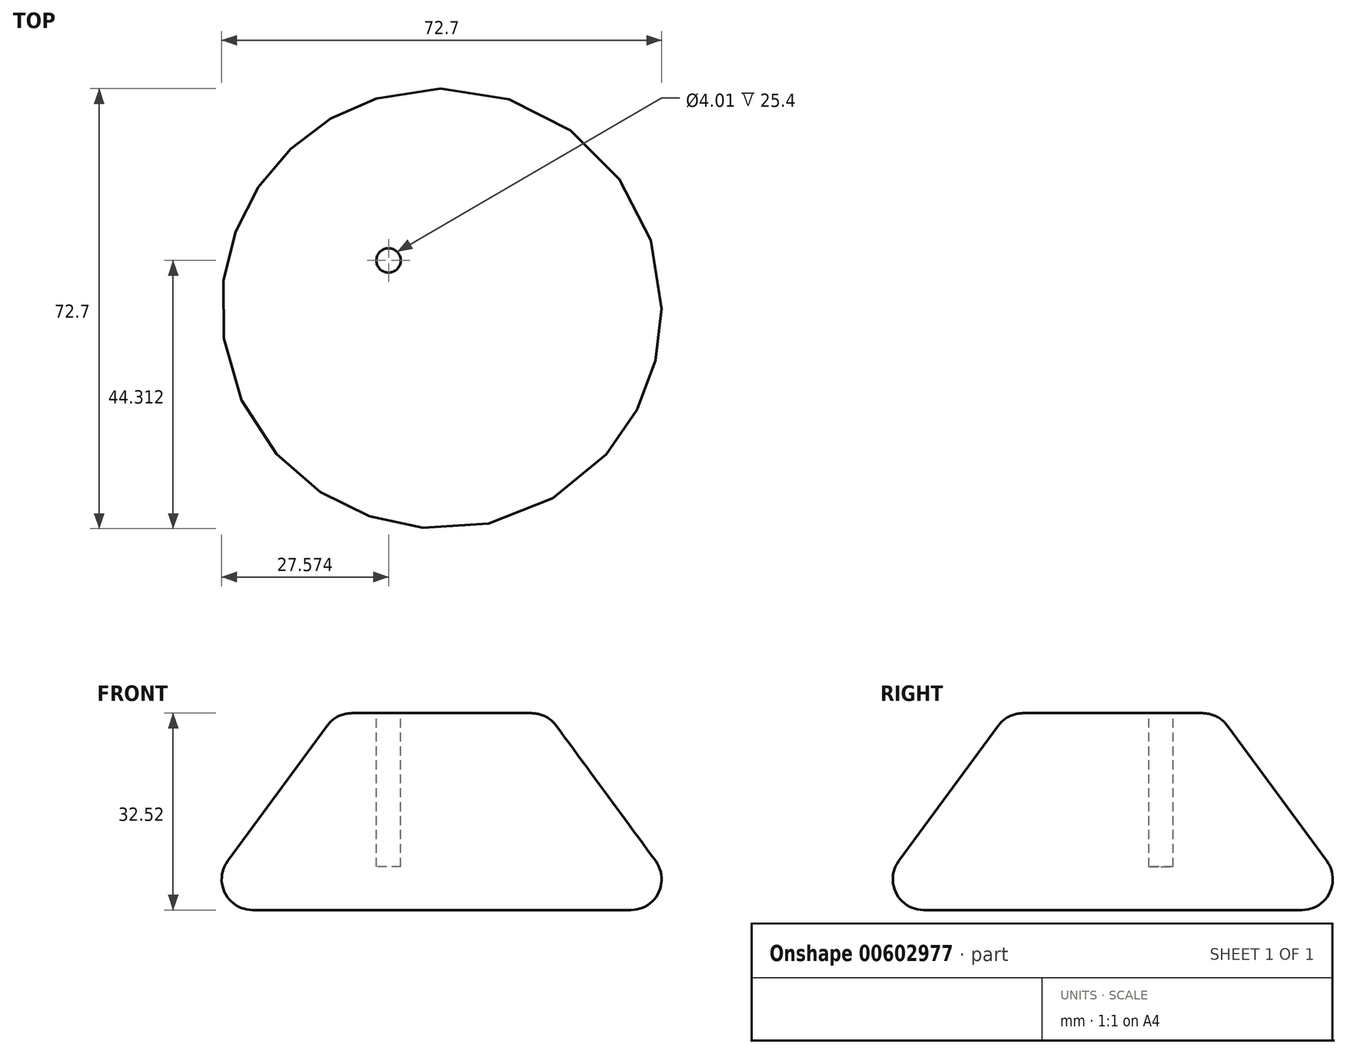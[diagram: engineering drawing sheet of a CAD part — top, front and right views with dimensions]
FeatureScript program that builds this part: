
annotation { "Feature Type Name" : "Feature", "Feature Type Description" : "" }
export const myFeature = defineFeature(function(context is Context, id is Id, definition is map)
    precondition{}
    {
        {
            var Q0;
            Q0=qCreatedBy(makeId("Front.planeOp"),FACE);
            var sketch = newSketch(context, id + "F0", { "sketchPlane" : qUnion([Q0])});
            skLineSegment(sketch, "E0", {"start": v(0, 55.7) * mm, "end": v(-17.41, 55.7) * mm});
            skLineSegment(sketch, "E1", {"start": v(-17.41, 55.7) * mm, "end": v(-41.3, 23.17) * mm});
            skLineSegment(sketch, "E2", {"start": v(-41.3, 23.17) * mm, "end": v(0, 23.17) * mm});
            skLineSegment(sketch, "E3", {"start": v(0, 23.17) * mm, "end": v(0, 55.7) * mm});
            skSolve(sketch);
        }
        {
            var Q0;
            Q0 = qSketchRegion(id + "F0", true);
            var Q1;
            Q1=sQuery(id+"F0.wireOp",EDGE,"E3");
            revolve(context, id + "F1", {"entities" : qUnion([Q0]), "axis" : qUnion([Q1]), "revolveType" : RevolveType.FULL});
        }
        {
            var Q0;
            Q0=makeQuery(id+"F1.opRevolve","SWEPT_EDGE",EDGE,{"disambiguationData":[OSD([sQuery(id+"F0.wireOp",EDGE,"E1"),sQuery(id+"F0.wireOp",EDGE,"E2")])]});
            var Q1;
            Q1=makeQuery(id+"F1.opRevolve","SWEPT_EDGE",EDGE,{"disambiguationData":[OSD([sQuery(id+"F0.wireOp",EDGE,"E0"),sQuery(id+"F0.wireOp",EDGE,"E1")])]});
            fillet(context, id + "F2", {"entities" : qUnion([Q0, Q1]), "radius" : 5.08 * mm, "tangentPropagation" : true, "allowEdgeOverflow" : false});
        }
        {
            var Q0;
            Q0=makeQuery(id+"F1.opRevolve","SWEPT_FACE",FACE,{"disambiguationData":[OSD([sQuery(id+"F0.wireOp",EDGE,"E0")])]});
            var sketch = newSketch(context, id + "F3", { "sketchPlane" : qUnion([Q0])});
            skCircle(sketch, "E4", {"center": v(-8.78, 7.96) * mm, "radius": 2 * mm});
            skSolve(sketch);
        }
        {
            var Q0;
            Q0=makeQuery(id+"F3.imprint","IMPRINT",FACE,{"disambiguationData":[TD([[makeQuery(id+"F3.imprint","IMPRINT",EDGE,{"derivedFrom":sQuery(id+"F3.wireOp",EDGE,"E4")}),1.0]])]});
            var Q1;
            Q1=sQuery(id+"F3.wireOp",EDGE,"E4");
            extrude(context, id + "F4", {"entities" : qUnion([Q0]), "operationType" : NewBodyOperationType.REMOVE, "surfaceEntities" : qUnion([Q1]), "oppositeDirection" : true, "depth" : 25.4 * mm, "offsetDistance" : 25.4 * mm});
        }
        {
            var Q0;
            Q0=qCreatedBy(makeId("Right.planeOp"),FACE);
            var sketch = newSketch(context, id + "F5", { "sketchPlane" : qUnion([Q0])});
            skLineSegment(sketch, "E5", {"start": v(0, 0) * mm, "end": v(0, 77.28) * mm, "construction": true});
            skSolve(sketch);
        }
    });
